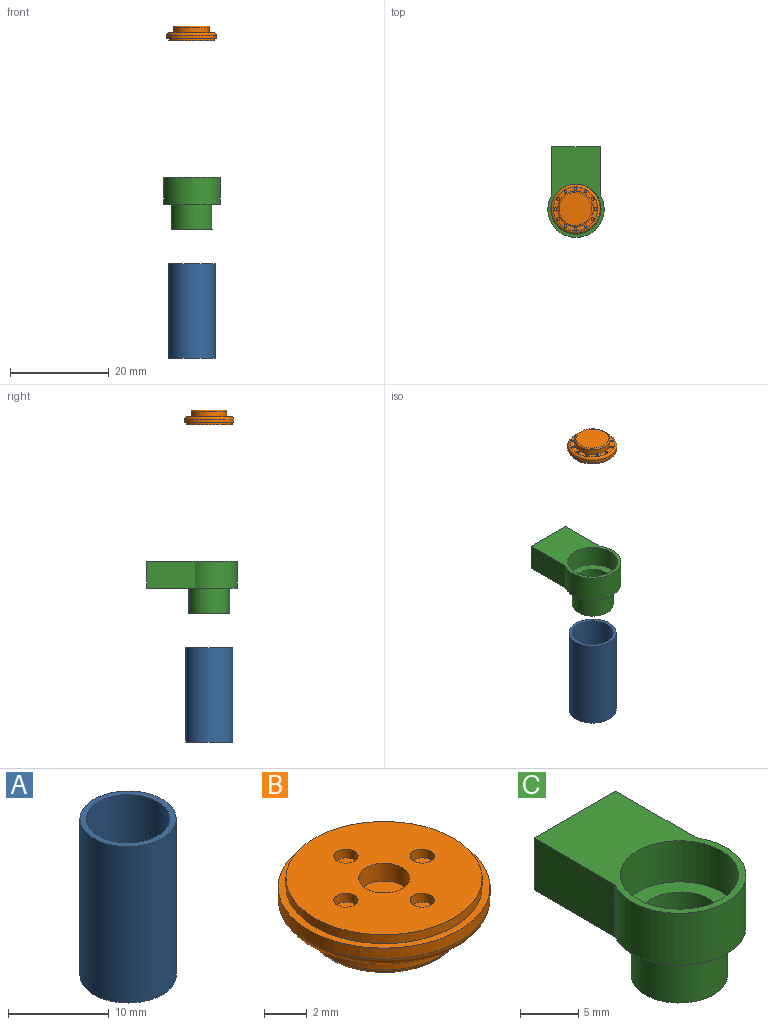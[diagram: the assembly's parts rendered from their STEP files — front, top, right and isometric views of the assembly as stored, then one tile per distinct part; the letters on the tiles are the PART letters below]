
ASSEMBLY  parts=3 mates=2
PART A: 4 faces, bbox 9.6x9.6x19.1 mm
  f0: cylinder r=4.15mm len=19.05mm, axis (0,0,-1), area 497.1mm2, adj f2,f3
  f1: cylinder r=4.79mm len=19.05mm, axis (0,0,-1), area 573.1mm2, adj f2,f3
  f2: plane 9.58x9.58mm, normal (0,0,1), area 17.8mm2, adj f0,f1
  f3: plane 9.58x9.58mm, normal (0,0,-1), area 17.8mm2, adj f0,f1
PART B: 43 faces, bbox 10.8x10.8x3 mm
  f0: cylinder r=3.58mm len=7.16mm, axis (0,0,1), area 25.1mm2, adj f3,f6
  f1: plane 6.65x6.65mm, normal (0,0,-1), area 34.8mm2, adj f6
  f2: cylinder r=4.99mm len=9.98mm, axis (0,0,1), area 19.9mm2, adj f4,f5
  f3: plane 8.97x8.97mm, normal (0,0,-1), area 19.8mm2, adj f0,f5,f7,f9,f11,f13,f15,f17
  f4: plane 9.98x9.98mm, normal (0,0,1), area 11.3mm2, adj f2,f32
  f5: torus R=4.48mm, axis (0,0,1), area 24.1mm2, adj f2,f3
  f6: torus R=3.33mm, axis (0,0,1), area 8.7mm2, adj f0,f1
  f7: cylinder r=0.28mm len=0.56mm, axis (0,0,-1), area 0.5mm2, adj f3,f8
  f8: plane 0.56x0.56mm, normal (0,0,-1), area 0.2mm2, adj f7
  f9: cylinder r=0.28mm len=0.56mm, axis (0,0,-1), area 0.5mm2, adj f3,f10
  f10: plane 0.56x0.56mm, normal (0,0,-1), area 0.2mm2, adj f9
  f11: cylinder r=0.28mm len=0.56mm, axis (0,0,-1), area 0.5mm2, adj f3,f12
  f12: plane 0.56x0.56mm, normal (0,0,-1), area 0.2mm2, adj f11
  f13: cylinder r=0.28mm len=0.56mm, axis (0,0,-1), area 0.5mm2, adj f3,f14
  f14: plane 0.56x0.56mm, normal (0,0,-1), area 0.2mm2, adj f13
  f15: cylinder r=0.28mm len=0.56mm, axis (0,0,-1), area 0.5mm2, adj f3,f16
  f16: plane 0.56x0.56mm, normal (0,0,-1), area 0.2mm2, adj f15
  f17: cylinder r=0.28mm len=0.56mm, axis (0,0,-1), area 0.5mm2, adj f3,f18
  f18: plane 0.56x0.56mm, normal (0,0,-1), area 0.2mm2, adj f17
  f19: cylinder r=0.28mm len=0.56mm, axis (0,0,-1), area 0.5mm2, adj f3,f20
  f20: plane 0.56x0.56mm, normal (0,0,-1), area 0.2mm2, adj f19
  f21: cylinder r=0.28mm len=0.56mm, axis (0,0,-1), area 0.5mm2, adj f3,f22
  f22: plane 0.56x0.56mm, normal (0,0,-1), area 0.2mm2, adj f21
  f23: cylinder r=0.28mm len=0.56mm, axis (0,0,-1), area 0.5mm2, adj f3,f24
  f24: plane 0.56x0.56mm, normal (0,0,-1), area 0.2mm2, adj f23
  f25: cylinder r=0.28mm len=0.56mm, axis (0,0,-1), area 0.5mm2, adj f3,f26
  f26: plane 0.56x0.56mm, normal (0,0,-1), area 0.2mm2, adj f25
  f27: cylinder r=0.28mm len=0.56mm, axis (0,0,-1), area 0.5mm2, adj f3,f28
  f28: plane 0.56x0.56mm, normal (0,0,-1), area 0.2mm2, adj f27
  f29: cylinder r=0.28mm len=0.56mm, axis (0,0,-1), area 0.5mm2, adj f3,f30
  f30: plane 0.56x0.56mm, normal (0,0,-1), area 0.2mm2, adj f29
  f31: plane 9.23x9.23mm, normal (0,0,1), area 58.3mm2, adj f32,f33,f35,f37,f39,f41
  f32: cylinder r=4.62mm len=9.23mm, axis (0,0,-1), area 14.7mm2, adj f4,f31
  f33: cylinder r=1.21mm len=2.41mm, axis (0,0,1), area 7.7mm2, adj f31,f34
  f34: plane 2.41x2.41mm, normal (0,0,1), area 4.6mm2, adj f33
  f35: cylinder r=0.57mm len=1.14mm, axis (0,0,1), area 1.8mm2, adj f31,f36
  f36: plane 1.14x1.14mm, normal (0,0,1), area 1mm2, adj f35
  f37: cylinder r=0.57mm len=1.14mm, axis (0,0,1), area 1.8mm2, adj f31,f38
  f38: plane 1.14x1.14mm, normal (0,0,1), area 1mm2, adj f37
  f39: cylinder r=0.57mm len=1.14mm, axis (0,0,1), area 1.8mm2, adj f31,f40
  f40: plane 1.14x1.14mm, normal (0,0,1), area 1mm2, adj f39
  f41: cylinder r=0.57mm len=1.14mm, axis (0,0,1), area 1.8mm2, adj f31,f42
  f42: plane 1.14x1.14mm, normal (0,0,1), area 1mm2, adj f41
PART C: 11 faces, bbox 11.4x18.4x10.5 mm
  f0: cylinder r=5.71mm len=11.43mm, axis (0,0,1), area 131mm2, adj f1,f2,f8,f10
  f1: plane 18.42x11.43mm, normal (0,0,-1), area 126.2mm2, adj f0,f6,f8,f9,f10
  f2: plane 18.42x11.43mm, normal (0,0,1), area 98.6mm2, adj f0,f3,f8,f9,f10
  f3: cylinder r=5.08mm len=10.16mm, axis (0,0,1), area 137.8mm2, adj f2,f4
  f4: plane 10.16x10.16mm, normal (0,0,1), area 42.8mm2, adj f3,f5
  f5: cylinder r=3.49mm len=6.99mm, axis (0,0,1), area 136.6mm2, adj f4,f7
  f6: cylinder r=4.13mm len=8.26mm, axis (0,0,1), area 131.7mm2, adj f1,f7
  f7: plane 8.26x8.26mm, normal (0,0,-1), area 15.2mm2, adj f5,f6
  f8: plane 9.82x5.46mm, normal (-1,0,0), area 53.6mm2, adj f0,f1,f2,f9
  f9: plane 9.87x5.46mm, normal (0,1,0), area 53.9mm2, adj f1,f2,f8,f10
  f10: plane 9.82x5.46mm, normal (1,0,0), area 53.6mm2, adj f0,f1,f2,f9
PLACE A t=(0,0,-35.35)mm
PLACE B rot(axis=(1,0,0),180deg) t=(-0.1,0,28.9)mm
PLACE C at identity fixed
MATE slider A.f0 <-> C.f6  axis (0,0,-1) through (0,0,-16.3)mm
MATE slider B.f2 <-> C.f4  axis (0,0,-1) through (-0.1,0,28.9)mm
